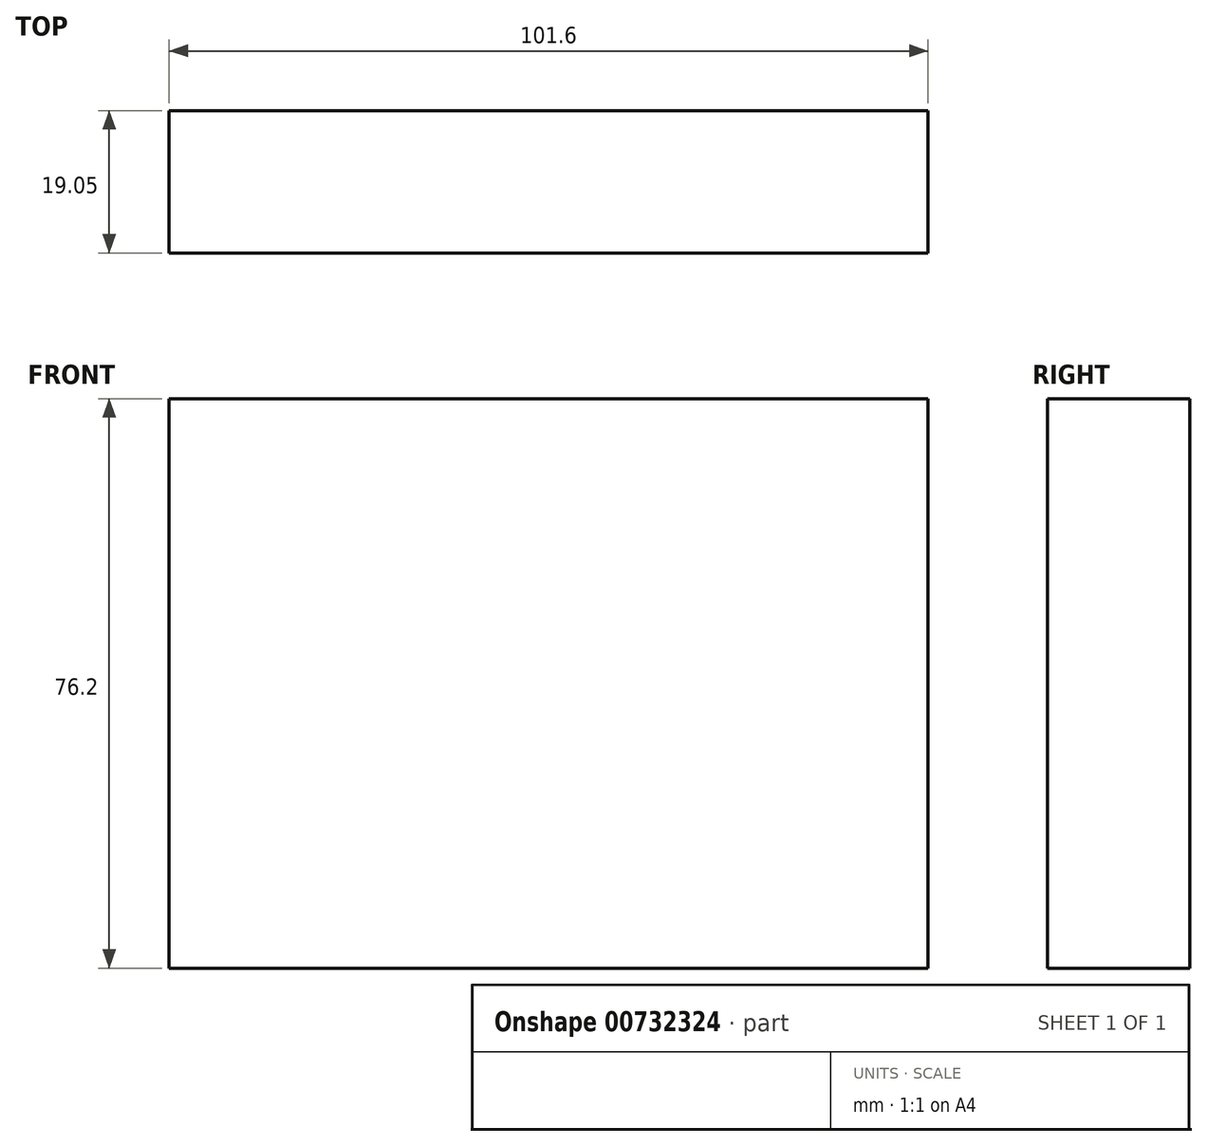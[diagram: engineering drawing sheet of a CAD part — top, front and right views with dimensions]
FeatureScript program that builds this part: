
annotation { "Feature Type Name" : "Feature", "Feature Type Description" : "" }
export const myFeature = defineFeature(function(context is Context, id is Id, definition is map)
    precondition{}
    {
        {
            var Q0;
            Q0=qCreatedBy(makeId("Front.planeOp"),FACE);
            var sketch = newSketch(context, id + "F0", { "sketchPlane" : qUnion([Q0])});
            skLineSegment(sketch, "E0.bottom", {"start": v(0, 0) * mm, "end": v(101.6, 0) * mm});
            skLineSegment(sketch, "E0.top", {"start": v(0, 76.2) * mm, "end": v(101.6, 76.2) * mm});
            skLineSegment(sketch, "E0.left", {"start": v(0, 0) * mm, "end": v(0, 76.2) * mm});
            skLineSegment(sketch, "E0.right", {"start": v(101.6, 0) * mm, "end": v(101.6, 76.2) * mm});
            skSolve(sketch);
        }
        {
            var Q0;
            Q0=qSketchRegion(id+"F0",true);
            extrude(context, id + "F1", {"entities" : qUnion([Q0]), "depth" : 19.05 * mm, "offsetDistance" : 25.4 * mm});
        }
    });
